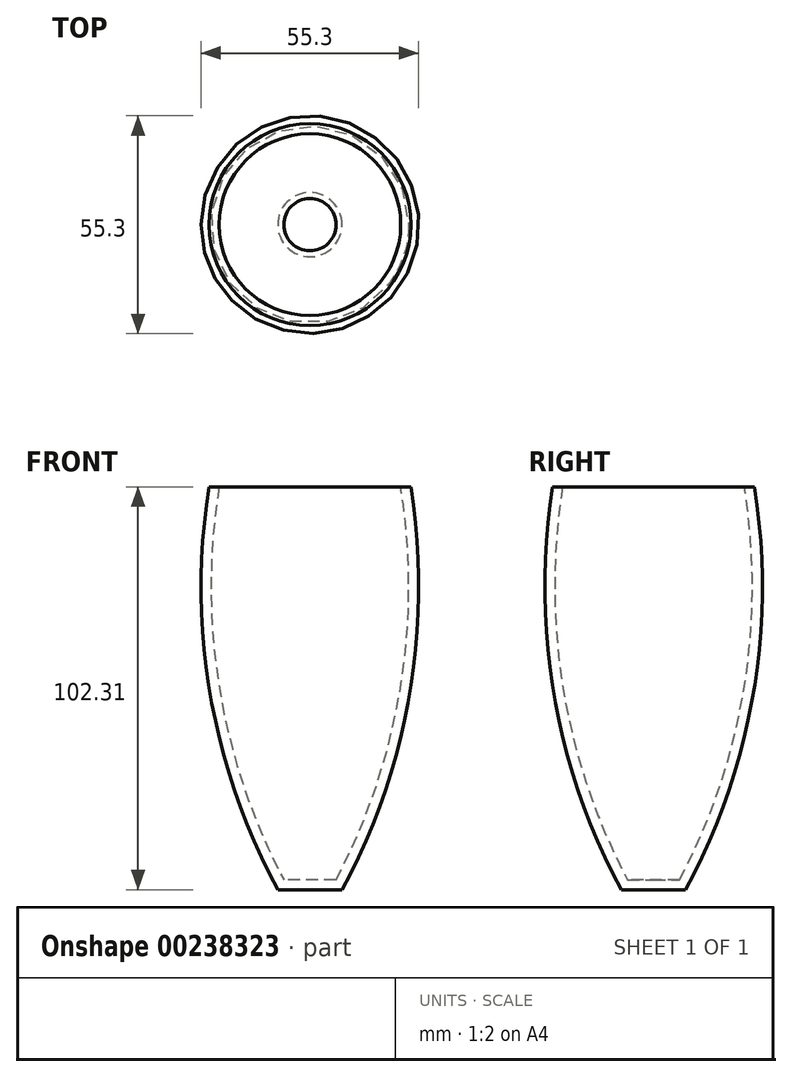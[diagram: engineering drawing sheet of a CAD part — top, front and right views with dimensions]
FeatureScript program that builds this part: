
annotation { "Feature Type Name" : "Feature", "Feature Type Description" : "" }
export const myFeature = defineFeature(function(context is Context, id is Id, definition is map)
    precondition{}
    {
        {
            var Q0;
            Q0=qCreatedBy(makeId("Front.planeOp"),FACE);
            var sketch = newSketch(context, id + "F0", { "sketchPlane" : qUnion([Q0])});
            skLineSegment(sketch, "E0", {"start": v(0, 56.4) * mm, "end": v(25.65, 56.4) * mm});
            skArc(sketch, "E1", {"start": v(8.16, -45.9) * mm, "mid": v(25.33, 3.8) * mm, "end": v(25.65, 56.4) * mm});
            skLineSegment(sketch, "E2", {"start": v(8.16, -45.9) * mm, "end": v(0, -45.9) * mm});
            skLineSegment(sketch, "E3", {"start": v(0, -45.9) * mm, "end": v(0, 56.4) * mm});
            skSolve(sketch);
        }
        {
            var Q0;
            Q0=makeQuery(id+"F0.imprint","IMPRINT",FACE,{"disambiguationData":[TD([[makeQuery(id+"F0.imprint","IMPRINT",EDGE,{"derivedFrom":sQuery(id+"F0.wireOp",EDGE,"E0")}),-1.0]])]});
            var Q1;
            Q1=sQuery(id+"F0.wireOp",EDGE,"E3");
            revolve(context, id + "F1", {"entities" : qUnion([Q0]), "axis" : qUnion([Q1]), "revolveType" : RevolveType.FULL});
        }
        {
            var Q0;
            Q0=makeQuery(id+"F1.opRevolve","SWEPT_FACE",FACE,{"disambiguationData":[OSD([sQuery(id+"F0.wireOp",EDGE,"E0")])]});
            shell(context, id + "F2", {"entities" : qUnion([Q0]), "thickness" : 2.54 * mm});
        }
    });
